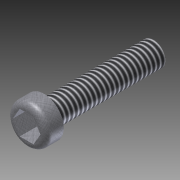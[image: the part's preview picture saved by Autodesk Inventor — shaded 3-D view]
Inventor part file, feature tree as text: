
AUTODESK INVENTOR PART (.ipt)
format: ipt  version: 2012 (Build 160160000, 160)  size: 109,568 bytes
history: native  units: in
note: dims shown in document units (in); Inventor stores cm internally (conversion verified against a paired STEP export)
features: extrude x2, sketch x1, thread x1, fillet x1
ambient origin geometry x8: Origin, YZ Plane, XZ Plane, XY Plane, X Axis, Y Axis, Z Axis, Center Point
bodies: Solid1 (feature_tree)
feature tree (5):
  sketch  "Sketch1"  dims[d0=0.164in d1=0.27in d2=1.0in d3=0.0in d4=0.12in d5=0.0in d6=1.0in d7=0.0in d8=0.04in]
  extrude  "Extrusion1"  Depth=0.27in
  extrude  "Extrusion2"  Depth=1.0in TaperAngle=0.0deg
  thread  "Thread1"  [1 undecoded]
  fillet  "Fillet1"  Radius=1.0in
note: 1 required parameter value undecoded (feature->parameter linkage not recoverable at this tier; creation-order binding heuristic only, values carry confidence <= 0.55)
